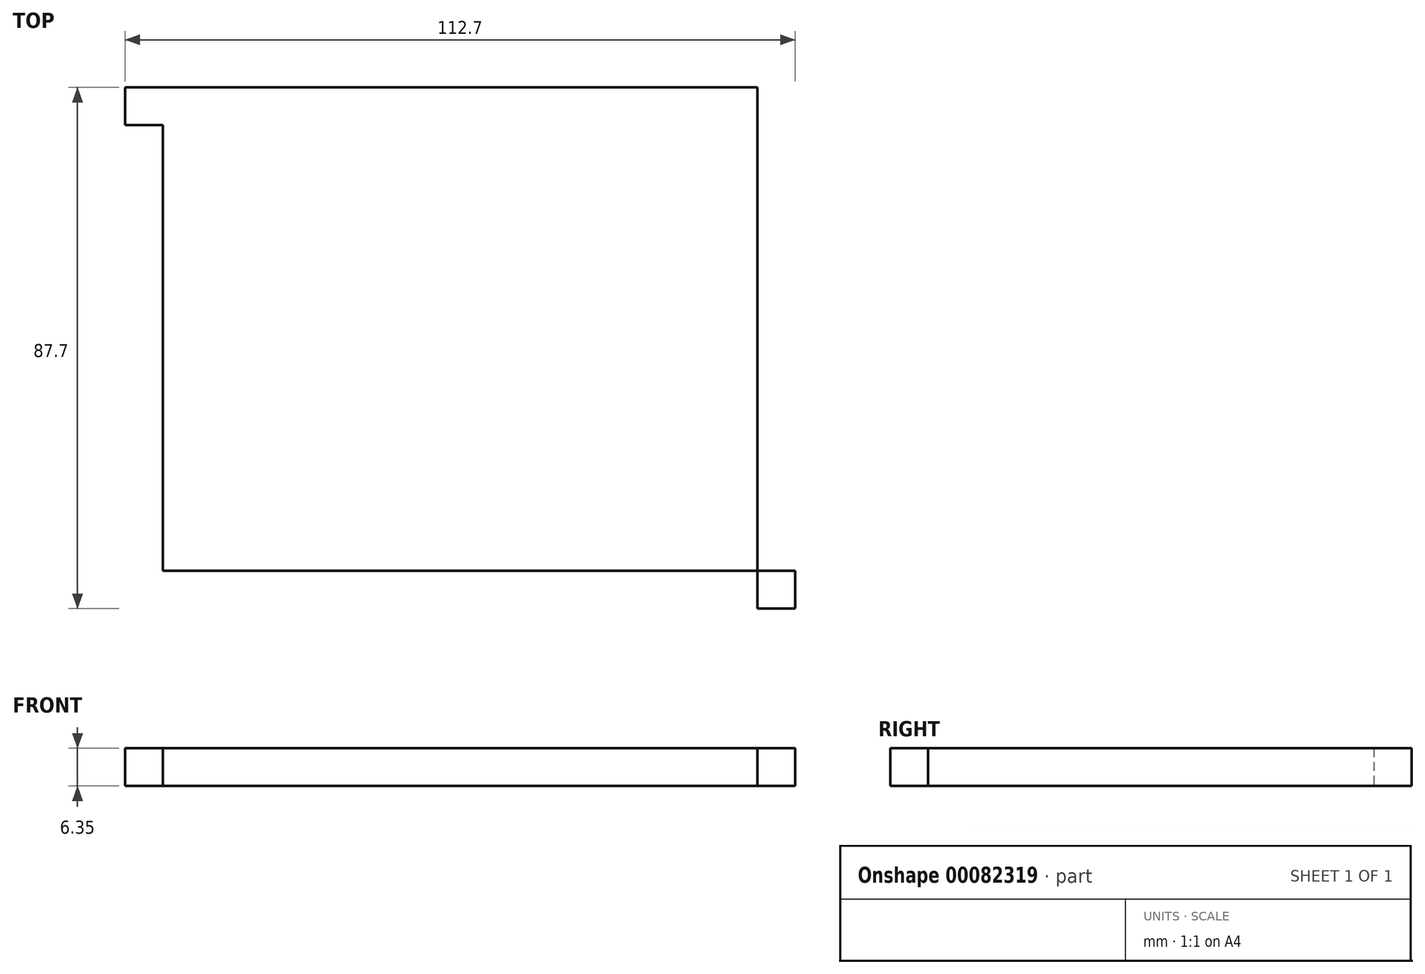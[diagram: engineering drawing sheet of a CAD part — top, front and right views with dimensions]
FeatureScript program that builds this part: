
annotation { "Feature Type Name" : "Feature", "Feature Type Description" : "" }
export const myFeature = defineFeature(function(context is Context, id is Id, definition is map)
    precondition{}
    {
        {
            var Q0;
            Q0=qCreatedBy(makeId("Top.planeOp"),FACE);
            var sketch = newSketch(context, id + "F0", { "sketchPlane" : qUnion([Q0])});
            skLineSegment(sketch, "E0.bottom", {"start": v(50, -37.5) * mm, "end": v(-50, -37.5) * mm});
            skLineSegment(sketch, "E0.top", {"start": v(50, 37.5) * mm, "end": v(-50, 37.5) * mm});
            skLineSegment(sketch, "E0.left", {"start": v(50, -37.5) * mm, "end": v(50, 37.5) * mm});
            skLineSegment(sketch, "E0.right", {"start": v(-50, -37.5) * mm, "end": v(-50, 37.5) * mm});
            skPoint(sketch, "E0.middle", {"position": v(0, 0) * mm});
            skLineSegment(sketch, "E1.bottom", {"start": v(20.5, -20.5) * mm, "end": v(-20.5, -20.5) * mm});
            skLineSegment(sketch, "E1.top", {"start": v(20.5, 20.5) * mm, "end": v(-20.5, 20.5) * mm});
            skLineSegment(sketch, "E1.left", {"start": v(20.5, -20.5) * mm, "end": v(20.5, 20.5) * mm});
            skLineSegment(sketch, "E1.right", {"start": v(-20.5, -20.5) * mm, "end": v(-20.5, 20.5) * mm});
            skLineSegment(sketch, "E2.top", {"start": v(50, 43.85) * mm, "end": v(-50, 43.85) * mm});
            skLineSegment(sketch, "E2.left", {"start": v(50, 37.5) * mm, "end": v(50, 43.85) * mm});
            skLineSegment(sketch, "E2.right", {"start": v(-50, 37.5) * mm, "end": v(-50, 43.85) * mm});
            skLineSegment(sketch, "E3.bottom", {"start": v(-50, 37.5) * mm, "end": v(-56.35, 37.5) * mm});
            skLineSegment(sketch, "E3.top", {"start": v(-50, 43.85) * mm, "end": v(-56.35, 43.85) * mm});
            skLineSegment(sketch, "E3.right", {"start": v(-56.35, 37.5) * mm, "end": v(-56.35, 43.85) * mm});
            skLineSegment(sketch, "E4.bottom", {"start": v(-50, -37.5) * mm, "end": v(50, -37.5) * mm});
            skLineSegment(sketch, "E4.top", {"start": v(-50, -43.85) * mm, "end": v(50, -43.85) * mm});
            skLineSegment(sketch, "E4.left", {"start": v(-50, -37.5) * mm, "end": v(-50, -43.85) * mm});
            skLineSegment(sketch, "E4.right", {"start": v(50, -37.5) * mm, "end": v(50, -43.85) * mm});
            skLineSegment(sketch, "E5.bottom", {"start": v(50, -37.5) * mm, "end": v(56.35, -37.5) * mm});
            skLineSegment(sketch, "E5.top", {"start": v(50, -43.85) * mm, "end": v(56.35, -43.85) * mm});
            skLineSegment(sketch, "E5.right", {"start": v(56.35, -37.5) * mm, "end": v(56.35, -43.85) * mm});
            skSolve(sketch);
        }
        {
            var Q0;
            Q0=makeQuery(id+"F0.imprint","IMPRINT",FACE,{"disambiguationData":[TD([[makeQuery(id+"F0.imprint","IMPRINT",EDGE,{"derivedFrom":sQuery(id+"F0.wireOp",EDGE,"E0.left")}),1.0]])]});
            var Q1;
            Q1=makeQuery(id+"F0.imprint","IMPRINT",FACE,{"disambiguationData":[TD([[makeQuery(id+"F0.imprint","IMPRINT",EDGE,{"derivedFrom":sQuery(id+"F0.wireOp",EDGE,"E0.top")}),-1.0]])]});
            var Q2;
            Q2=makeQuery(id+"F0.imprint","IMPRINT",FACE,{"disambiguationData":[TD([[makeQuery(id+"F0.imprint","IMPRINT",EDGE,{"derivedFrom":sQuery(id+"F0.wireOp",EDGE,"E3.bottom")}),-1.0]])]});
            var Q3;
            Q3=makeQuery(id+"F0.imprint","IMPRINT",FACE,{"disambiguationData":[TD([[makeQuery(id+"F0.imprint","IMPRINT",EDGE,{"derivedFrom":sQuery(id+"F0.wireOp",EDGE,"E4.bottom")}),-1.0]])]});
            var Q4;
            Q4=makeQuery(id+"F0.imprint","IMPRINT",FACE,{"disambiguationData":[TD([[makeQuery(id+"F0.imprint","IMPRINT",EDGE,{"derivedFrom":sQuery(id+"F0.wireOp",EDGE,"E5.bottom")}),-1.0]])]});
            var Q5;
            Q5=makeQuery(id+"F0.imprint","IMPRINT",FACE,{"disambiguationData":[TD([[makeQuery(id+"F0.imprint","IMPRINT",EDGE,{"derivedFrom":sQuery(id+"F0.wireOp",EDGE,"E1.bottom")}),-1.0]])]});
            extrude(context, id + "F1", {"entities" : qUnion([Q0, Q1, Q2, Q3, Q4, Q5]), "depth" : 6.35 * mm});
        }
    });
